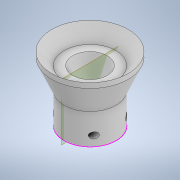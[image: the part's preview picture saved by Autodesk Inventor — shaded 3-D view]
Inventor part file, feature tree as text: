
AUTODESK INVENTOR PART (.ipt)
format: ipt  version: 2020 (Build 240168000, 168)  size: 174,592 bytes
history: native  units: in
note: dims shown in document units (in); Inventor stores cm internally (conversion verified against a paired STEP export)
features: sketch x4, hole x2, revolve x1, plane x1
ambient origin geometry x8: Origin, YZ Plane, XZ Plane, XY Plane, X Axis, Y Axis, Z Axis, Center Point
bodies: Solid1 (feature_tree)
feature tree (8):
  revolve  "Revolution1"  [1 undecoded]
  hole  "Hole1"  [1 undecoded]
  sketch  "Sketch3"  dims[d16=45.0deg d17=90.0deg]
  plane  "Work Plane1"
  hole  "Hole2"  [1 undecoded]
  sketch  "Sketch1"  dims[d7=90.0deg d8=0.211in]
  sketch  "Sketch2"  dims[d10=0.375in d11=0.25in d12=0.5635in d13=0.375in d14=0.0in d15=0.325in]
  sketch  "Sketch4"  dims[d18=0.4in d19=45.0deg d20=0.4in d21=135.0deg d22=0.177in d23=0.328in d24=0.332in d25=0.25in d26=0.5635in d27=0.484in d28=0.8108in d29=0.725in d30=0.389in d31=45.0deg d32=0.5in d33=45.0deg d34=0.146in d35=180.0deg]
note: 3 required parameter values undecoded (feature->parameter linkage not recoverable at this tier; creation-order binding heuristic only, values carry confidence <= 0.55)